# Revit family: Lighting-StreetLighting-GEWISS-STREET[O3]-DOUBLE_HEAD_BRACKET
name_source: partatom
category: Apparecchi per illuminazione
units: mm (PartAtom-declared; Revit-internal decimal feet)

## family parameters
Basato su piano di lavoro = Sì
Condiviso = No
Numero OmniClass = 23.80.00.00
Punto di calcolo locali = No
Quota connettore circolare = Usa diametro
Sempre verticale = No
Sorgente d'illuminazione = No
Taglio con vuoti quando caricato = No
Tipo di parte = Normale
Titolo OmniClass = Electric Power and Lighting

## types (1)
- GW87582 - Galvanised steel - Grey - Double
    Altezza da terra testa staffa = 822 mm
    Catalogue = LIGHTING
    Catalogue Range = STREET [O3]
    Colour = Graphite grey
    Description: = Double pole head bracket
    Descrizione = STREET DOUBLE POLE HEAD BRACKET GR. GREY
    Dimension = Ã˜ 60mm
    Dimensions (mm) = Ã˜ 60mm
    EAN code = 8011564783041
    Electrocod = 240
    IDF = 7e945946-5768-40a6-be54-5c9846dae879
    IDT = df385655-572c-45cd-afe2-85265a4e7826
    Immagine tipo = GW87582.jpg
    L_staffa = 120 mm  [stored 0.393701 ft]
    Length = 1+1 m
    Material = Galvanised steel
    Modello = GW87582
    Produttore = GEWISS S.p.A.
    Prospetto di default = 1219 mm
    SEO = Bracket
    Supporti = <Per categoria>
    Technical sheet = https://www.gewiss.com
    Tubolare = <Per categoria>
    URL = https://www.gewiss.com
    Version file RFA = 20.11
    Weight (kg) = 11,5
    Weight (kg): = 11,5

note: [stored X ft] marks values corroborated as IEEE doubles in the binary element streams (Revit-internal decimal feet)

## geometry (parser evidence)
native form markers: Blend x4
no freeform markers — native parametric forms only
